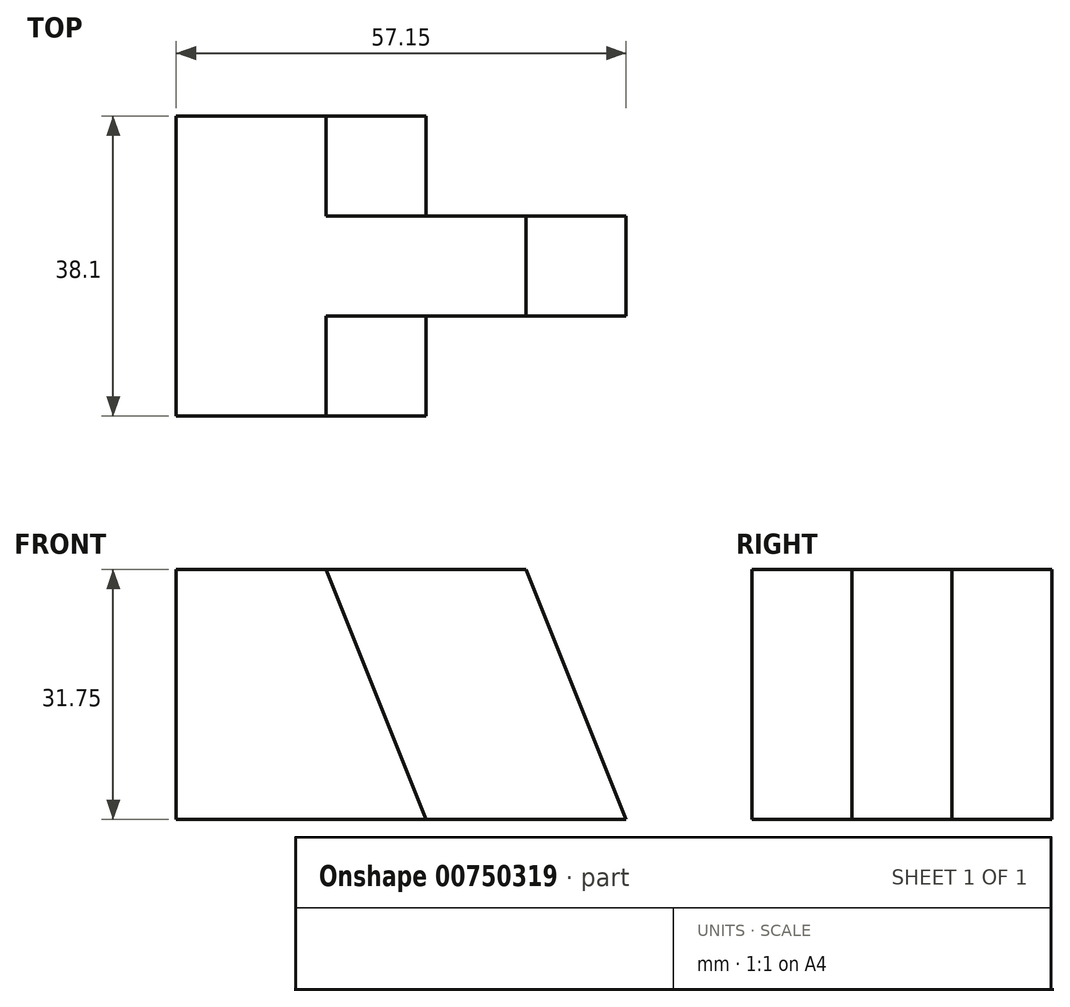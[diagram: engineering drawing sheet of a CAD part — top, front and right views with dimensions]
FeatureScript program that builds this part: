
annotation { "Feature Type Name" : "Feature", "Feature Type Description" : "" }
export const myFeature = defineFeature(function(context is Context, id is Id, definition is map)
    precondition{}
    {
        {
            var Q0;
            Q0=qCreatedBy(makeId("Top.planeOp"),FACE);
            var sketch = newSketch(context, id + "F0", { "sketchPlane" : qUnion([Q0])});
            skLineSegment(sketch, "E0", {"start": v(0, 0) * mm, "end": v(0, 38.1) * mm});
            skLineSegment(sketch, "E1", {"start": v(0, 38.1) * mm, "end": v(19.05, 38.1) * mm});
            skLineSegment(sketch, "E2", {"start": v(19.05, 38.1) * mm, "end": v(19.05, 25.4) * mm});
            skLineSegment(sketch, "E3", {"start": v(19.05, 25.4) * mm, "end": v(44.45, 25.4) * mm});
            skLineSegment(sketch, "E4", {"start": v(44.45, 25.4) * mm, "end": v(44.45, 12.7) * mm});
            skLineSegment(sketch, "E5", {"start": v(44.45, 12.7) * mm, "end": v(19.05, 12.7) * mm});
            skLineSegment(sketch, "E6", {"start": v(19.05, 12.7) * mm, "end": v(19.05, 0) * mm});
            skLineSegment(sketch, "E7", {"start": v(19.05, 0) * mm, "end": v(0, 0) * mm});
            skSolve(sketch);
        }
        {
            var Q0;
            Q0 = qSketchRegion(id + "F0", true);
            extrude(context, id + "F1", {"entities" : qUnion([Q0]), "depth" : 31.75 * mm, "offsetDistance" : 25.4 * mm});
        }
        {
            var Q0;
            Q0=makeQuery(id+"F1.opExtrude","SWEPT_FACE",FACE,{"disambiguationData":[OSD([sQuery(id+"F0.wireOp",EDGE,"E5")])]});
            var sketch = newSketch(context, id + "F2", { "sketchPlane" : qUnion([Q0])});
            skLineSegment(sketch, "E8", {"start": v(19.05, 31.75) * mm, "end": v(31.75, 0) * mm});
            skLineSegment(sketch, "E9", {"start": v(31.75, 0) * mm, "end": v(19.05, 0) * mm});
            skLineSegment(sketch, "E10", {"start": v(19.05, 0) * mm, "end": v(19.05, 31.75) * mm});
            skSolve(sketch);
        }
        {
            var Q0;
            Q0=makeQuery(id+"F2.imprint","IMPRINT",FACE,{"disambiguationData":[TD([[makeQuery(id+"F2.imprint","IMPRINT",EDGE,{"derivedFrom":sQuery(id+"F2.wireOp",EDGE,"E8")}),-1.0]])]});
            extrude(context, id + "F3", {"entities" : qUnion([Q0]), "operationType" : NewBodyOperationType.ADD, "depth" : 12.7 * mm, "offsetDistance" : 25.4 * mm});
        }
        {
            var Q0;
            Q0=makeQuery(id+"F1.opExtrude","SWEPT_FACE",FACE,{"disambiguationData":[OSD([sQuery(id+"F0.wireOp",EDGE,"E3")])]});
            var sketch = newSketch(context, id + "F4", { "sketchPlane" : qUnion([Q0])});
            skLineSegment(sketch, "E11", {"start": v(-44.45, 31.75) * mm, "end": v(-57.15, 0) * mm});
            skLineSegment(sketch, "E12", {"start": v(-57.15, 0) * mm, "end": v(-44.45, 0) * mm});
            skLineSegment(sketch, "E13", {"start": v(-44.45, 0) * mm, "end": v(-44.45, 31.75) * mm});
            skSolve(sketch);
        }
        {
            var Q0;
            Q0 = qSketchRegion(id + "F4", true);
            extrude(context, id + "F5", {"entities" : qUnion([Q0]), "operationType" : NewBodyOperationType.ADD, "oppositeDirection" : true, "depth" : 12.7 * mm, "offsetDistance" : 25.4 * mm});
        }
        {
            var Q0;
            Q0=makeQuery(id+"F5.boolean.opBoolean","MERGE",FACE,{"derivedFrom":[makeQuery(id+"F1.opExtrude","SWEPT_FACE",FACE,{"disambiguationData":[OSD([sQuery(id+"F0.wireOp",EDGE,"E3")])]}),makeQuery(id+"F5.opExtrude","CAP_FACE",FACE,{"disambiguationData":[OSD([sQuery(id+"F4.wireOp",EDGE,"E11"),sQuery(id+"F4.wireOp",EDGE,"E12"),sQuery(id+"F4.wireOp",EDGE,"E13")])],"isStart":true})]});
            var sketch = newSketch(context, id + "F6", { "sketchPlane" : qUnion([Q0])});
            skLineSegment(sketch, "E14", {"start": v(-19.05, 31.75) * mm, "end": v(-31.75, 0) * mm});
            skPoint(sketch, "E14.endSnap0", {"position": v(-31.75, 31.75) * mm});
            skLineSegment(sketch, "E15", {"start": v(-31.75, 0) * mm, "end": v(-19.05, 0) * mm});
            skLineSegment(sketch, "E16", {"start": v(-19.05, 0) * mm, "end": v(-19.05, 31.75) * mm});
            skSolve(sketch);
        }
        {
            var Q0;
            Q0 = qSketchRegion(id + "F6", true);
            extrude(context, id + "F7", {"entities" : qUnion([Q0]), "operationType" : NewBodyOperationType.ADD, "depth" : 12.7 * mm, "offsetDistance" : 25.4 * mm});
        }
    });
